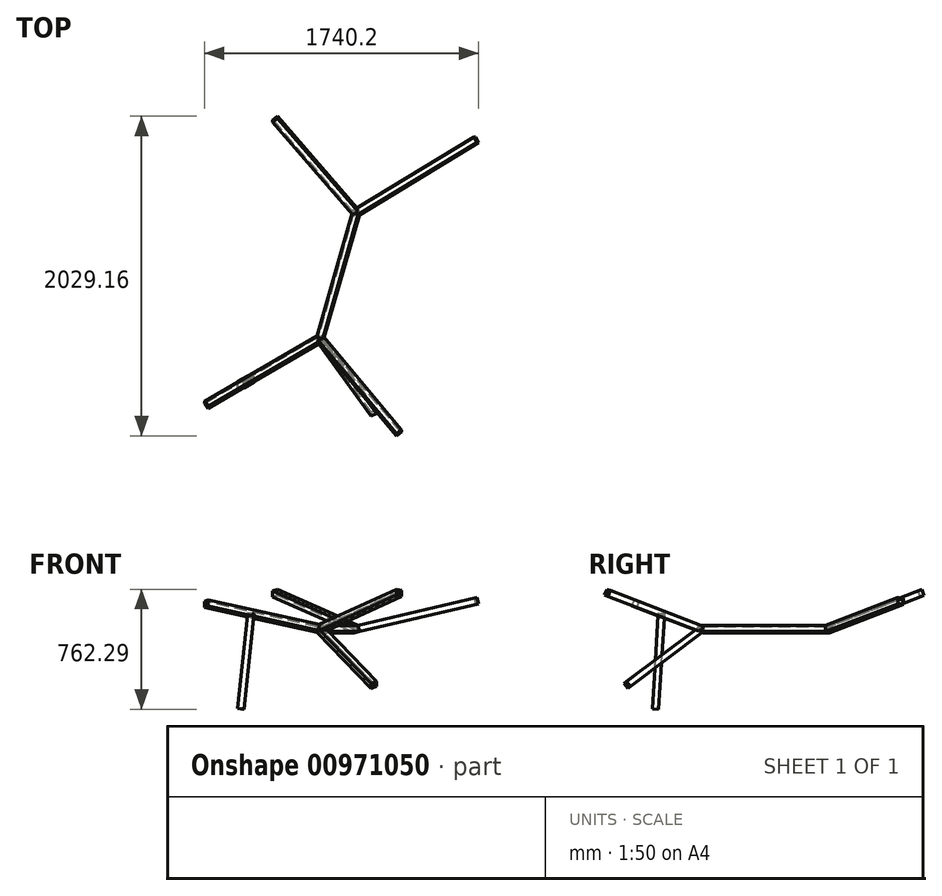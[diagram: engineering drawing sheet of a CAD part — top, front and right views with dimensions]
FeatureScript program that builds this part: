
annotation { "Feature Type Name" : "Feature", "Feature Type Description" : "" }
export const myFeature = defineFeature(function(context is Context, id is Id, definition is map)
    precondition{}
    {
        {
            var Q0;
            Q0=qCreatedBy(makeId("Right.planeOp"),FACE);
            var sketch = newSketch(context, id + "F0", { "sketchPlane" : qUnion([Q0])});
            skLineSegment(sketch, "E0", {"start": v(0, 0) * mm, "end": v(74.69, 28.67) * mm});
            skSolve(sketch);
        }
        {
            var Q0;
            Q0=sQuery(id+"F0.wireOp",EDGE,"E0");
            cPlane(context, id + "F1", {"entities" : qUnion([Q0]), "cplaneType" : CPlaneType.LINE_ANGLE, "offset" : 25 * mm, "angle" : 0 * degree, "width" : 150 * mm, "height" : 150 * mm});
        }
        {
            var Q0;
            Q0=qCreatedBy(id+"F1.planeOp",FACE);
            var sketch = newSketch(context, id + "F2", { "sketchPlane" : qUnion([Q0])});
            skLineSegment(sketch, "E1", {"start": v(0, 0) * mm, "end": v(-514.78, 635.7) * mm});
            skLineSegment(sketch, "E2", {"start": v(0, 0) * mm, "end": v(764.03, 496.17) * mm});
            skLineSegment(sketch, "E3", {"start": v(0, 0) * mm, "end": v(0, 572.11) * mm, "construction": true});
            skSolve(sketch);
        }
        {
            var Q0;
            Q0=sQuery(id+"F2.wireOp",EDGE,"E1");
            var Q1;
            Q1=sQuery(id+"F2.wireOp",VERTEX,"E1.end");
            cPlane(context, id + "F3", {"entities" : qUnion([Q0, Q1]), "cplaneType" : CPlaneType.LINE_POINT, "offset" : 25 * mm, "width" : 150 * mm, "height" : 150 * mm});
        }
        {
            var Q0;
            Q0=sQuery(id+"F2.wireOp",EDGE,"E2");
            var Q1;
            Q1=sQuery(id+"F2.wireOp",VERTEX,"E2.end");
            cPlane(context, id + "F4", {"entities" : qUnion([Q0, Q1]), "cplaneType" : CPlaneType.LINE_POINT, "offset" : 25 * mm, "width" : 150 * mm, "height" : 150 * mm});
        }
        {
            var Q0;
            Q0=qCreatedBy(id+"F3.planeOp",FACE);
            var sketch = newSketch(context, id + "F5", { "sketchPlane" : qUnion([Q0])});
            skLineSegment(sketch, "E4.bottom", {"start": v(20, -20) * mm, "end": v(-20, -20) * mm});
            skLineSegment(sketch, "E4.top", {"start": v(20, 20) * mm, "end": v(-20, 20) * mm});
            skLineSegment(sketch, "E4.left", {"start": v(20, -20) * mm, "end": v(20, 20) * mm});
            skLineSegment(sketch, "E4.right", {"start": v(-20, -20) * mm, "end": v(-20, 20) * mm});
            skPoint(sketch, "E4.middle", {"position": v(0, 0) * mm});
            skLineSegment(sketch, "E5.0", {"start": v(-18, -18) * mm, "end": v(-18, 18) * mm});
            skLineSegment(sketch, "E5.1", {"start": v(18, -18) * mm, "end": v(-18, -18) * mm});
            skLineSegment(sketch, "E5.2", {"start": v(18, -18) * mm, "end": v(18, 18) * mm});
            skLineSegment(sketch, "E5.3", {"start": v(18, 18) * mm, "end": v(-18, 18) * mm});
            skSolve(sketch);
        }
        {
            var Q0;
            Q0=qCreatedBy(id+"F4.planeOp",FACE);
            var sketch = newSketch(context, id + "F6", { "sketchPlane" : qUnion([Q0])});
            skLineSegment(sketch, "E6.bottom", {"start": v(20, 20) * mm, "end": v(-20, 20) * mm});
            skLineSegment(sketch, "E6.top", {"start": v(20, -20) * mm, "end": v(-20, -20) * mm});
            skLineSegment(sketch, "E6.left", {"start": v(20, 20) * mm, "end": v(20, -20) * mm});
            skLineSegment(sketch, "E6.right", {"start": v(-20, 20) * mm, "end": v(-20, -20) * mm});
            skPoint(sketch, "E6.middle", {"position": v(0, 0) * mm});
            skLineSegment(sketch, "E7.0", {"start": v(18, 18) * mm, "end": v(-18, 18) * mm});
            skLineSegment(sketch, "E7.1", {"start": v(18, 18) * mm, "end": v(18, -18) * mm});
            skLineSegment(sketch, "E7.2", {"start": v(18, -18) * mm, "end": v(-18, -18) * mm});
            skLineSegment(sketch, "E7.3", {"start": v(-18, 18) * mm, "end": v(-18, -18) * mm});
            skSolve(sketch);
        }
        {
            var Q0;
            Q0=qCreatedBy(makeId("Top.planeOp"),FACE);
            var sketch = newSketch(context, id + "F7", { "sketchPlane" : qUnion([Q0])});
            skLineSegment(sketch, "E8", {"start": v(0, 0) * mm, "end": v(-229, -800) * mm});
            skSolve(sketch);
        }
        {
            var Q0;
            Q0=qCreatedBy(makeId("Right.planeOp"),FACE);
            var sketch = newSketch(context, id + "F8", { "sketchPlane" : qUnion([Q0])});
            skLineSegment(sketch, "E9", {"start": v(-800, 0) * mm, "end": v(-874.69, 28.67) * mm});
            skSolve(sketch);
        }
        {
            var Q0;
            Q0=sQuery(id+"F8.wireOp",EDGE,"E9");
            cPlane(context, id + "F9", {"entities" : qUnion([Q0]), "cplaneType" : CPlaneType.LINE_ANGLE, "offset" : 25 * mm, "angle" : 0 * degree, "width" : 150 * mm, "height" : 150 * mm});
        }
        {
            var Q0;
            Q0=qCreatedBy(id+"F9.planeOp",FACE);
            var sketch = newSketch(context, id + "F10", { "sketchPlane" : qUnion([Q0])});
            skLineSegment(sketch, "E10", {"start": v(-950.69, 1197.83) * mm, "end": v(-229, 746.86) * mm});
            skLineSegment(sketch, "E11", {"start": v(-229, 746.86) * mm, "end": v(271.53, 1387.52) * mm});
            skLineSegment(sketch, "E12", {"start": v(-229, 746.86) * mm, "end": v(-229, 1400.13) * mm, "construction": true});
            skSolve(sketch);
        }
        {
            var Q0;
            Q0=makeQuery(id+"F6.imprint","IMPRINT",FACE,{"disambiguationData":[TD([[makeQuery(id+"F6.imprint","IMPRINT",EDGE,{"derivedFrom":sQuery(id+"F6.wireOp",EDGE,"E6.bottom")}),1.0]])]});
            var Q1;
            Q1=sQuery(id+"F2.wireOp",EDGE,"E2");
            var Q2;
            Q2=sQuery(id+"F7.wireOp",EDGE,"E8");
            var Q3;
            Q3=sQuery(id+"F10.wireOp",EDGE,"E10");
            sweep(context, id + "F11", {"profiles" : qUnion([Q0]), "path" : qUnion([Q1, Q2, Q3])});
        }
        {
            var Q0;
            Q0=sQuery(id+"F10.wireOp",EDGE,"E11");
            var Q1;
            Q1=sQuery(id+"F10.wireOp",VERTEX,"E11.end");
            cPlane(context, id + "F12", {"entities" : qUnion([Q0, Q1]), "cplaneType" : CPlaneType.LINE_POINT, "offset" : 25 * mm, "width" : 150 * mm, "height" : 150 * mm});
        }
        {
            var Q0;
            Q0=qCreatedBy(id+"F12.planeOp",FACE);
            var sketch = newSketch(context, id + "F13", { "sketchPlane" : qUnion([Q0])});
            skLineSegment(sketch, "E13.bottom", {"start": v(-620.27, -266.7) * mm, "end": v(-660.27, -266.7) * mm});
            skLineSegment(sketch, "E13.top", {"start": v(-620.27, -306.7) * mm, "end": v(-660.27, -306.7) * mm});
            skLineSegment(sketch, "E13.left", {"start": v(-620.27, -266.7) * mm, "end": v(-620.27, -306.7) * mm});
            skLineSegment(sketch, "E13.right", {"start": v(-660.27, -266.7) * mm, "end": v(-660.27, -306.7) * mm});
            skPoint(sketch, "E13.middle", {"position": v(-640.27, -286.7) * mm});
            skLineSegment(sketch, "E14.0", {"start": v(-658.27, -268.7) * mm, "end": v(-658.27, -304.7) * mm});
            skLineSegment(sketch, "E14.1", {"start": v(-622.27, -268.7) * mm, "end": v(-658.27, -268.7) * mm});
            skLineSegment(sketch, "E14.2", {"start": v(-622.27, -268.7) * mm, "end": v(-622.27, -304.7) * mm});
            skLineSegment(sketch, "E14.3", {"start": v(-622.27, -304.7) * mm, "end": v(-658.27, -304.7) * mm});
            skSolve(sketch);
        }
        {
            var Q0;
            Q0=makeQuery(id+"F5.imprint","IMPRINT",FACE,{"disambiguationData":[TD([[makeQuery(id+"F5.imprint","IMPRINT",EDGE,{"derivedFrom":sQuery(id+"F5.wireOp",EDGE,"E4.bottom")}),-1.0]])]});
            var Q1;
            Q1=sQuery(id+"F2.wireOp",EDGE,"E1");
            sweep(context, id + "F14", {"operationType" : NewBodyOperationType.ADD, "profiles" : qUnion([Q0]), "path" : qUnion([Q1])});
        }
        {
            var Q0;
            Q0=makeQuery(id+"F13.imprint","IMPRINT",FACE,{"disambiguationData":[TD([[makeQuery(id+"F13.imprint","IMPRINT",EDGE,{"derivedFrom":sQuery(id+"F13.wireOp",EDGE,"E13.bottom")}),1.0]])]});
            var Q1;
            Q1=sQuery(id+"F10.wireOp",EDGE,"E11");
            sweep(context, id + "F15", {"operationType" : NewBodyOperationType.ADD, "profiles" : qUnion([Q0]), "path" : qUnion([Q1])});
        }
        {
            var Q0;
            Q0=qCreatedBy(makeId("Right.planeOp"),FACE);
            var sketch = newSketch(context, id + "F16", { "sketchPlane" : qUnion([Q0])});
            skLineSegment(sketch, "E15", {"start": v(-800, 0) * mm, "end": v(-863.9, -48.15) * mm});
            skSolve(sketch);
        }
        {
            var Q0;
            Q0=sQuery(id+"F16.wireOp",EDGE,"E15");
            cPlane(context, id + "F17", {"entities" : qUnion([Q0]), "cplaneType" : CPlaneType.LINE_ANGLE, "offset" : 25 * mm, "angle" : 0 * degree, "width" : 150 * mm, "height" : 150 * mm});
        }
        {
            var Q0;
            Q0=qCreatedBy(id+"F17.planeOp",FACE);
            var sketch = newSketch(context, id + "F18", { "sketchPlane" : qUnion([Q0])});
            skLineSegment(sketch, "E16", {"start": v(-229, 638.9) * mm, "end": v(112.5, 1230.4) * mm});
            skLineSegment(sketch, "E17", {"start": v(-229, 638.9) * mm, "end": v(-229, 1175.5) * mm, "construction": true});
            skSolve(sketch);
        }
        {
            var Q0;
            Q0=sQuery(id+"F18.wireOp",EDGE,"E16");
            var Q1;
            Q1=sQuery(id+"F18.wireOp",VERTEX,"E16.end");
            cPlane(context, id + "F19", {"entities" : qUnion([Q0, Q1]), "cplaneType" : CPlaneType.LINE_POINT, "offset" : 25 * mm, "width" : 150 * mm, "height" : 150 * mm});
        }
        {
            var Q0;
            Q0=qCreatedBy(id+"F19.planeOp",FACE);
            var sketch = newSketch(context, id + "F20", { "sketchPlane" : qUnion([Q0])});
            skLineSegment(sketch, "E18.bottom", {"start": v(-497.77, 501.45) * mm, "end": v(-537.77, 501.45) * mm});
            skLineSegment(sketch, "E18.top", {"start": v(-497.77, 461.45) * mm, "end": v(-537.77, 461.45) * mm});
            skLineSegment(sketch, "E18.left", {"start": v(-497.77, 501.45) * mm, "end": v(-497.77, 461.45) * mm});
            skLineSegment(sketch, "E18.right", {"start": v(-537.77, 501.45) * mm, "end": v(-537.77, 461.45) * mm});
            skPoint(sketch, "E18.middle", {"position": v(-517.77, 481.45) * mm});
            skLineSegment(sketch, "E19.0", {"start": v(-499.77, 499.45) * mm, "end": v(-535.77, 499.45) * mm});
            skLineSegment(sketch, "E19.1", {"start": v(-499.77, 499.45) * mm, "end": v(-499.77, 463.45) * mm});
            skLineSegment(sketch, "E19.2", {"start": v(-499.77, 463.45) * mm, "end": v(-535.77, 463.45) * mm});
            skLineSegment(sketch, "E19.3", {"start": v(-535.77, 499.45) * mm, "end": v(-535.77, 463.45) * mm});
            skSolve(sketch);
        }
        {
            var Q0;
            Q0=makeQuery(id+"F20.imprint","IMPRINT",FACE,{"disambiguationData":[TD([[makeQuery(id+"F20.imprint","IMPRINT",EDGE,{"derivedFrom":sQuery(id+"F20.wireOp",EDGE,"E18.bottom")}),1.0]])]});
            var Q1;
            Q1=sQuery(id+"F18.wireOp",EDGE,"E16");
            sweep(context, id + "F21", {"operationType" : NewBodyOperationType.ADD, "profiles" : qUnion([Q0]), "path" : qUnion([Q1])});
        }
        {
            var Q0;
            Q0=sQuery(id+"F10.wireOp",EDGE,"E10");
            cPlane(context, id + "F22", {"entities" : qUnion([Q0]), "cplaneType" : CPlaneType.LINE_ANGLE, "offset" : 25 * mm, "angle" : 0 * degree, "width" : 150 * mm, "height" : 150 * mm});
        }
        {
            var Q0;
            Q0=qCreatedBy(id+"F22.planeOp",FACE);
            var sketch = newSketch(context, id + "F23", { "sketchPlane" : qUnion([Q0])});
            skLineSegment(sketch, "E20", {"start": v(1108.7, 98.22) * mm, "end": v(1182.35, -506.31) * mm});
            skSolve(sketch);
        }
        {
            var Q0;
            Q0=sQuery(id+"F23.wireOp",EDGE,"E20");
            var Q1;
            Q1=sQuery(id+"F23.wireOp",VERTEX,"E20.end");
            cPlane(context, id + "F24", {"entities" : qUnion([Q0, Q1]), "cplaneType" : CPlaneType.LINE_POINT, "offset" : 25 * mm, "width" : 150 * mm, "height" : 150 * mm});
        }
        {
            var Q0;
            Q0=qCreatedBy(id+"F24.planeOp",FACE);
            var sketch = newSketch(context, id + "F25", { "sketchPlane" : qUnion([Q0])});
            skLineSegment(sketch, "E21.bottom", {"start": v(-647.43, 1079.9) * mm, "end": v(-687.43, 1079.9) * mm});
            skLineSegment(sketch, "E21.top", {"start": v(-647.43, 1039.9) * mm, "end": v(-687.43, 1039.9) * mm});
            skLineSegment(sketch, "E21.left", {"start": v(-647.43, 1079.9) * mm, "end": v(-647.43, 1039.9) * mm});
            skLineSegment(sketch, "E21.right", {"start": v(-687.43, 1079.9) * mm, "end": v(-687.43, 1039.9) * mm});
            skPoint(sketch, "E21.middle", {"position": v(-667.43, 1059.9) * mm});
            skLineSegment(sketch, "E22.0", {"start": v(-649.43, 1077.9) * mm, "end": v(-685.43, 1077.9) * mm});
            skLineSegment(sketch, "E22.1", {"start": v(-649.43, 1077.9) * mm, "end": v(-649.43, 1041.9) * mm});
            skLineSegment(sketch, "E22.2", {"start": v(-649.43, 1041.9) * mm, "end": v(-685.43, 1041.9) * mm});
            skLineSegment(sketch, "E22.3", {"start": v(-685.43, 1077.9) * mm, "end": v(-685.43, 1041.9) * mm});
            skSolve(sketch);
        }
        {
            var Q0;
            Q0=makeQuery(id+"F25.imprint","IMPRINT",FACE,{"disambiguationData":[TD([[makeQuery(id+"F25.imprint","IMPRINT",EDGE,{"derivedFrom":sQuery(id+"F25.wireOp",EDGE,"E21.bottom")}),1.0]])]});
            var Q1;
            Q1=sQuery(id+"F23.wireOp",EDGE,"E20");
            sweep(context, id + "F26", {"operationType" : NewBodyOperationType.ADD, "profiles" : qUnion([Q0]), "path" : qUnion([Q1])});
        }
    });
